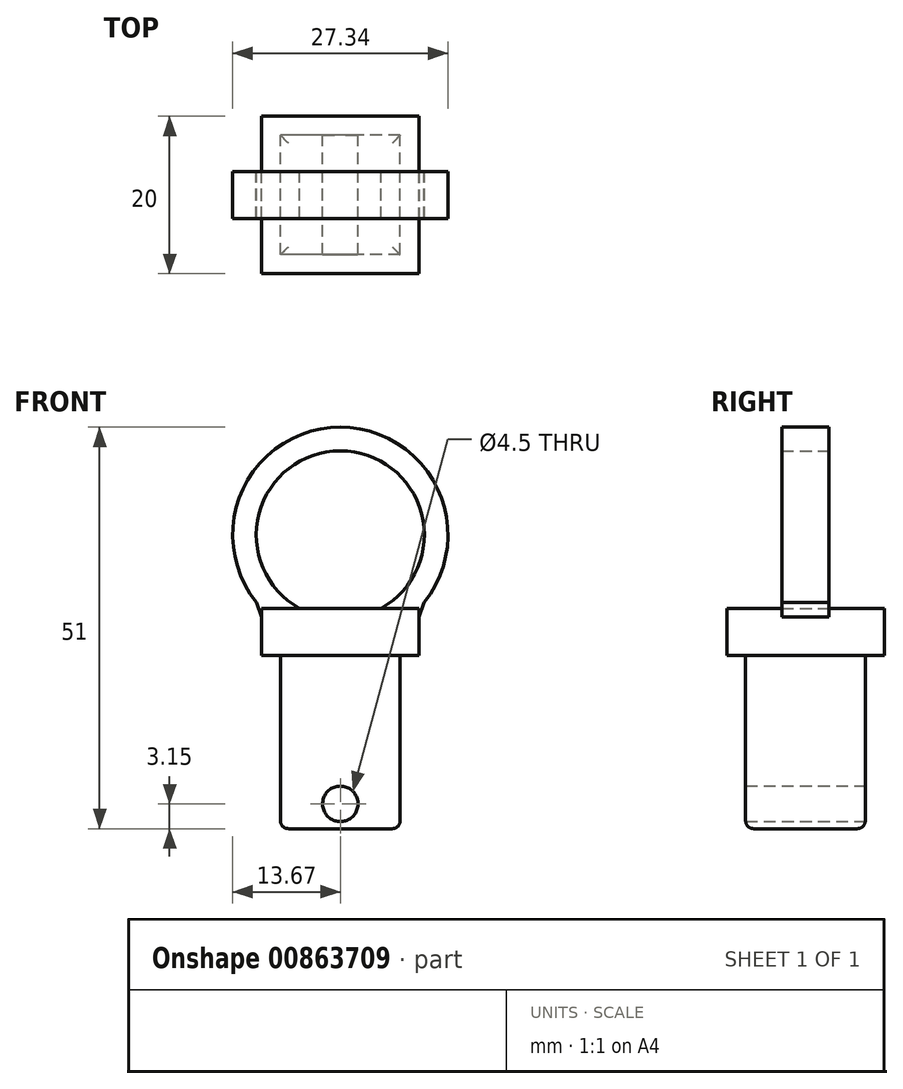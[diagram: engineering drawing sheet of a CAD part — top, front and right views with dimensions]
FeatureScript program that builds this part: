
annotation { "Feature Type Name" : "Feature", "Feature Type Description" : "" }
export const myFeature = defineFeature(function(context is Context, id is Id, definition is map)
    precondition{}
    {
        {
            var Q0;
            Q0=qCreatedBy(makeId("Front.planeOp"),FACE);
            var sketch = newSketch(context, id + "F0", { "sketchPlane" : qUnion([Q0])});
            skLineSegment(sketch, "E0.bottom", {"start": v(10, 3) * mm, "end": v(-10, 3) * mm});
            skLineSegment(sketch, "E0.top", {"start": v(10, -3) * mm, "end": v(-10, -3) * mm});
            skLineSegment(sketch, "E0.left", {"start": v(10, 3) * mm, "end": v(10, -3) * mm});
            skLineSegment(sketch, "E0.right", {"start": v(-10, 3) * mm, "end": v(-10, -3) * mm});
            skPoint(sketch, "E0.middle", {"position": v(0, 0) * mm});
            skArc(sketch, "E1", {"start": v(10, 3) * mm, "mid": v(0, 26) * mm, "end": v(-10, 3) * mm});
            skArc(sketch, "E2.0", {"start": v(5.2, 3) * mm, "mid": v(0, 23) * mm, "end": v(-5.2, 3) * mm});
            skLineSegment(sketch, "E3.bottom", {"start": v(7.6, -3) * mm, "end": v(-7.6, -3) * mm});
            skLineSegment(sketch, "E3.top", {"start": v(7.6, -25) * mm, "end": v(-7.6, -25) * mm});
            skLineSegment(sketch, "E3.left", {"start": v(7.6, -3) * mm, "end": v(7.6, -25) * mm});
            skLineSegment(sketch, "E3.right", {"start": v(-7.6, -3) * mm, "end": v(-7.6, -25) * mm});
            skPoint(sketch, "E3.middle", {"position": v(0, -14) * mm});
            skCircle(sketch, "E4", {"center": v(0, -21.85) * mm, "radius": 2.25 * mm});
            skSolve(sketch);
        }
        {
            var Q0;
            Q0=makeQuery(id+"F0.imprint","IMPRINT",FACE,{"disambiguationData":[TD([[makeQuery(id+"F0.imprint","IMPRINT",EDGE,{"derivedFrom":sQuery(id+"F0.wireOp",EDGE,"E3.top")}),-1.0]])]});
            extrude(context, id + "F1", {"entities" : qUnion([Q0]), "endBound" : BoundingType.SYMMETRIC, "depth" : 15.2 * mm, "offsetDistance" : 25 * mm});
        }
        {
            var Q0;
            {var subQ9=sQuery(id+"F0.wireOp",EDGE,"E0.left");Q0=makeQuery(id+"F0.imprint","IMPRINT",FACE,{"disambiguationData":[TD([[makeQuery(id+"F0.imprint","IMPRINT",EDGE,{"derivedFrom":subQ9}),-1.0]])]});}
            extrude(context, id + "F2", {"entities" : qUnion([Q0]), "operationType" : NewBodyOperationType.ADD, "endBound" : BoundingType.SYMMETRIC, "depth" : 20 * mm, "offsetDistance" : 25 * mm});
        }
        {
            var Q0;
            {var subQ2=sQuery(id+"F0.wireOp",EDGE,"E1");Q0=makeQuery(id+"F0.imprint","IMPRINT",FACE,{"disambiguationData":[TD([[makeQuery(id+"F0.imprint","IMPRINT",EDGE,{"derivedFrom":subQ2}),1.0]])]});}
            extrude(context, id + "F3", {"entities" : qUnion([Q0]), "operationType" : NewBodyOperationType.ADD, "endBound" : BoundingType.SYMMETRIC, "depth" : 6 * mm, "offsetDistance" : 25 * mm});
        }
        {
            var Q0;
            {var subQ0=sQuery(id+"F0.wireOp",EDGE,"E0.bottom");Q0=makeQuery(id+"F3.opExtrude","CAP_EDGE",EDGE,{"disambiguationData":[OSD([subQ0]),TDD([makeQuery(id+"F0.imprint","IMPRINT",EDGE,{"disambiguationData":[TD([[makeQuery(id+"F0.imprint","INTERSECT",VERTEX,{"disambiguationData":[OD(1.0)],"derivedFrom":[subQ0,sQuery(id+"F0.wireOp",EDGE,"E2.0")]}),-1.0]])],"derivedFrom":subQ0})])],"isStart":false});}
            var Q1;
            {var subQ0=sQuery(id+"F0.wireOp",EDGE,"E2.0");var subQ1=sQuery(id+"F0.wireOp",EDGE,"E0.bottom");Q1=makeQuery(id+"F3.opExtrude","SWEPT_EDGE",EDGE,{"disambiguationData":[OSD([subQ1,subQ0]),TDD([makeQuery(id+"F0.imprint","INTERSECT",VERTEX,{"disambiguationData":[OD(1.0)],"derivedFrom":[subQ1,subQ0]})])]});}
            var Q2;
            {var subQ0=sQuery(id+"F0.wireOp",EDGE,"E0.bottom");Q2=makeQuery(id+"F3.opExtrude","CAP_EDGE",EDGE,{"disambiguationData":[OSD([subQ0]),TDD([makeQuery(id+"F0.imprint","IMPRINT",EDGE,{"disambiguationData":[TD([[makeQuery(id+"F0.imprint","INTERSECT",VERTEX,{"disambiguationData":[OD(1.0)],"derivedFrom":[subQ0,sQuery(id+"F0.wireOp",EDGE,"E2.0")]}),-1.0]])],"derivedFrom":subQ0})])],"isStart":true});}
            var Q3;
            {var subQ0=sQuery(id+"F0.wireOp",EDGE,"E1");var subQ1=sQuery(id+"F0.wireOp",EDGE,"E0.right");var subQ2=sQuery(id+"F0.wireOp",EDGE,"E0.bottom");Q3=makeQuery(id+"F3.boolean.opBoolean","MERGE",EDGE,{"derivedFrom":[makeQuery(id+"F2.opExtrude","SWEPT_EDGE",EDGE,{"disambiguationData":[OSD([subQ2,subQ1,subQ0])]}),makeQuery(id+"F3.opExtrude","SWEPT_EDGE",EDGE,{"disambiguationData":[OSD([subQ2,subQ1,subQ0])]})]});}
            var Q4;
            {var subQ0=sQuery(id+"F0.wireOp",EDGE,"E2.0");var subQ1=sQuery(id+"F0.wireOp",EDGE,"E0.bottom");Q4=makeQuery(id+"F3.opExtrude","SWEPT_EDGE",EDGE,{"disambiguationData":[OSD([subQ1,subQ0]),TDD([makeQuery(id+"F0.imprint","INTERSECT",VERTEX,{"disambiguationData":[OD(0.0)],"derivedFrom":[subQ1,subQ0]})])]});}
            var Q5;
            {var subQ0=sQuery(id+"F0.wireOp",EDGE,"E0.bottom");Q5=makeQuery(id+"F3.opExtrude","CAP_EDGE",EDGE,{"disambiguationData":[OSD([subQ0]),TDD([makeQuery(id+"F0.imprint","IMPRINT",EDGE,{"disambiguationData":[TD([[makeQuery(id+"F0.imprint","INTERSECT",VERTEX,{"disambiguationData":[OD(0.0)],"derivedFrom":[subQ0,sQuery(id+"F0.wireOp",EDGE,"E2.0")]}),1.0]])],"derivedFrom":subQ0})])],"isStart":false});}
            var Q6;
            {var subQ0=sQuery(id+"F0.wireOp",EDGE,"E1");var subQ1=sQuery(id+"F0.wireOp",EDGE,"E0.left");var subQ2=sQuery(id+"F0.wireOp",EDGE,"E0.bottom");Q6=makeQuery(id+"F3.boolean.opBoolean","MERGE",EDGE,{"derivedFrom":[makeQuery(id+"F2.opExtrude","SWEPT_EDGE",EDGE,{"disambiguationData":[OSD([subQ2,subQ1,subQ0])]}),makeQuery(id+"F3.opExtrude","SWEPT_EDGE",EDGE,{"disambiguationData":[OSD([subQ2,subQ1,subQ0])]})]});}
            var Q7;
            {var subQ0=sQuery(id+"F0.wireOp",EDGE,"E0.bottom");Q7=makeQuery(id+"F3.opExtrude","CAP_EDGE",EDGE,{"disambiguationData":[OSD([subQ0]),TDD([makeQuery(id+"F0.imprint","IMPRINT",EDGE,{"disambiguationData":[TD([[makeQuery(id+"F0.imprint","INTERSECT",VERTEX,{"disambiguationData":[OD(0.0)],"derivedFrom":[subQ0,sQuery(id+"F0.wireOp",EDGE,"E2.0")]}),1.0]])],"derivedFrom":subQ0})])],"isStart":true});}
            chamfer(context, id + "F4", {"entities" : qUnion([Q0, Q1, Q2, Q3, Q4, Q5, Q6, Q7]), "width" : 3 * mm, "tangentPropagation" : true});
        }
        {
            var Q0;
            Q0=makeQuery(id+"F1.opExtrude","CAP_EDGE",EDGE,{"disambiguationData":[OSD([sQuery(id+"F0.wireOp",EDGE,"E3.top")])],"isStart":false});
            var Q1;
            Q1=makeQuery(id+"F1.opExtrude","SWEPT_EDGE",EDGE,{"disambiguationData":[OSD([sQuery(id+"F0.wireOp",EDGE,"E3.top"),sQuery(id+"F0.wireOp",EDGE,"E3.left")])]});
            var Q2;
            Q2=makeQuery(id+"F1.opExtrude","CAP_EDGE",EDGE,{"disambiguationData":[OSD([sQuery(id+"F0.wireOp",EDGE,"E3.top")])],"isStart":true});
            var Q3;
            Q3=makeQuery(id+"F1.opExtrude","SWEPT_EDGE",EDGE,{"disambiguationData":[OSD([sQuery(id+"F0.wireOp",EDGE,"E3.top"),sQuery(id+"F0.wireOp",EDGE,"E3.right")])]});
            fillet(context, id + "F5", {"entities" : qUnion([Q0, Q1, Q2, Q3]), "radius" : 1 * mm, "tangentPropagation" : true, "allowEdgeOverflow" : false});
        }
    });
